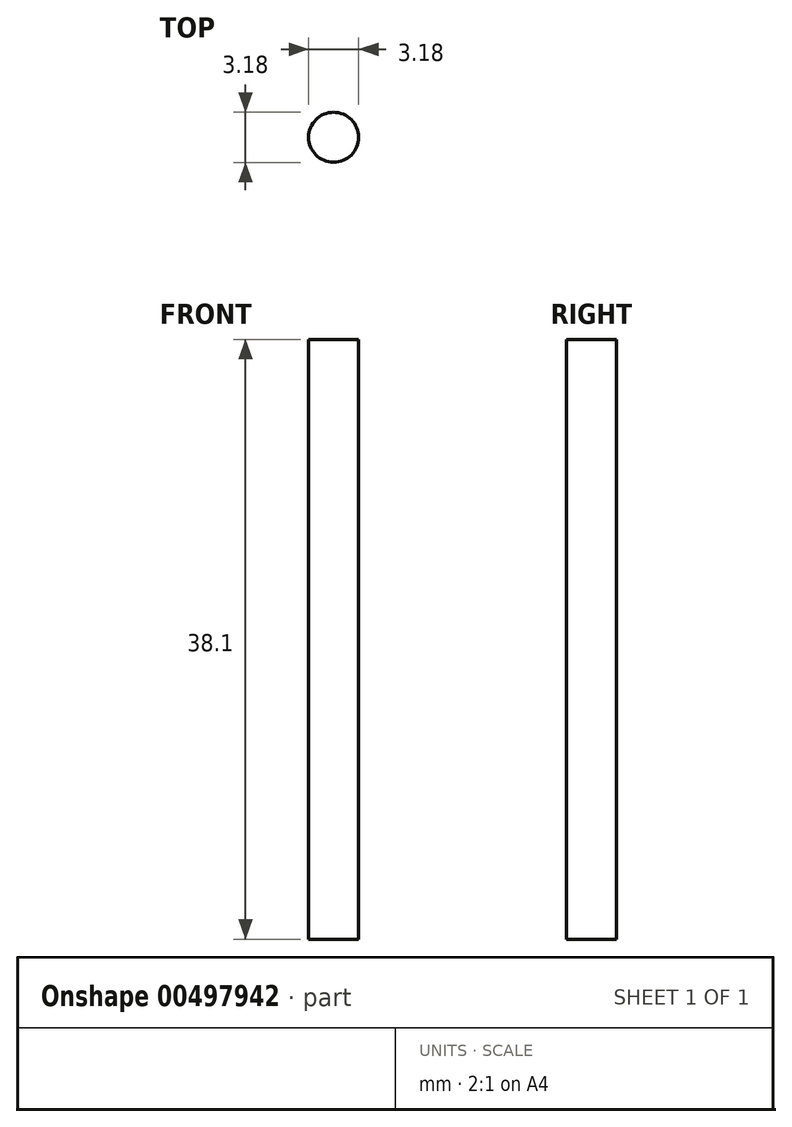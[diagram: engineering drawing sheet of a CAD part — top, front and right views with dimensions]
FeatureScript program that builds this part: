
annotation { "Feature Type Name" : "Feature", "Feature Type Description" : "" }
export const myFeature = defineFeature(function(context is Context, id is Id, definition is map)
    precondition{}
    {
        {
            var Q0;
            Q0=qCreatedBy(makeId("Top.planeOp"),FACE);
            var sketch = newSketch(context, id + "F0", { "sketchPlane" : qUnion([Q0])});
            skCircle(sketch, "E0", {"center": v(0, 0) * mm, "radius": 1.59 * mm});
            skSolve(sketch);
        }
        {
            var Q0;
            Q0 = qSketchRegion(id + "F0", true);
            extrude(context, id + "F1", {"entities" : qUnion([Q0]), "depth" : 38.1 * mm});
        }
    });
